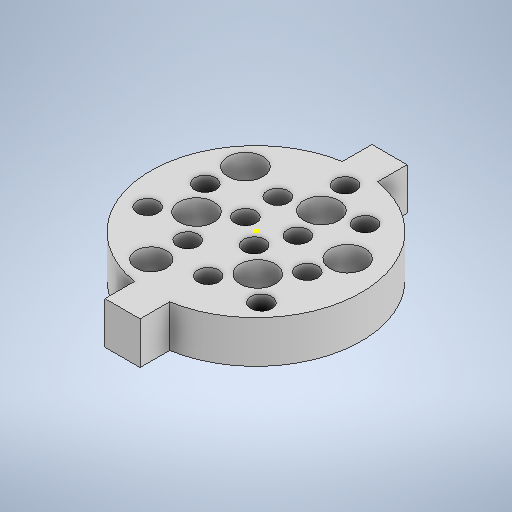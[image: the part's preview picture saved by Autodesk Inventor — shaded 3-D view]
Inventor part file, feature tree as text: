
AUTODESK INVENTOR PART (.ipt)
format: ipt  version: 2025.2 (Build 292293000, 293)  size: 313,344 bytes
history: native  units: in
note: dims shown in document units (in); Inventor stores cm internally (conversion verified against a paired STEP export)
features: sketch x6, extrude x2
ambient origin geometry x8: Origin, YZ Plane, XZ Plane, XY Plane, X Axis, Y Axis, Z Axis, Center Point
bodies: Solid1 (feature_tree)
feature tree (8):
  extrude  "Extrusion1"  Depth=0.0984in
  extrude  "Extrusion2"  Depth=0.1969in TaperAngle=0.0deg
  sketch  "Sketch3"  dims[d15=1.5748in]
  sketch  "Sketch1"  dims[d0=0.1575in d1=0.0984in]
  sketch  "Sketch2"  dims[d2=0.2362in d3=0.0in d11=0.1969in d12=0.0in]
  sketch  "Sketch Circular Pattern2"  dims[d13=1.1811in]
  sketch  "Sketch Circular Pattern3"  dims[d16=0.1969in d17=0.3937in d18=0.1181in d19=360.0deg]
  sketch  "Sketch Circular Pattern5"  dims[d21=1.5748in d22=0.1969in d23=0.3937in d24=0.1181in d25=360.0deg d33=1.5748in d34=0.1969in d35=0.3937in d36=0.1181in d37=360.0deg d38=0.1969in d39=0.1969in]
